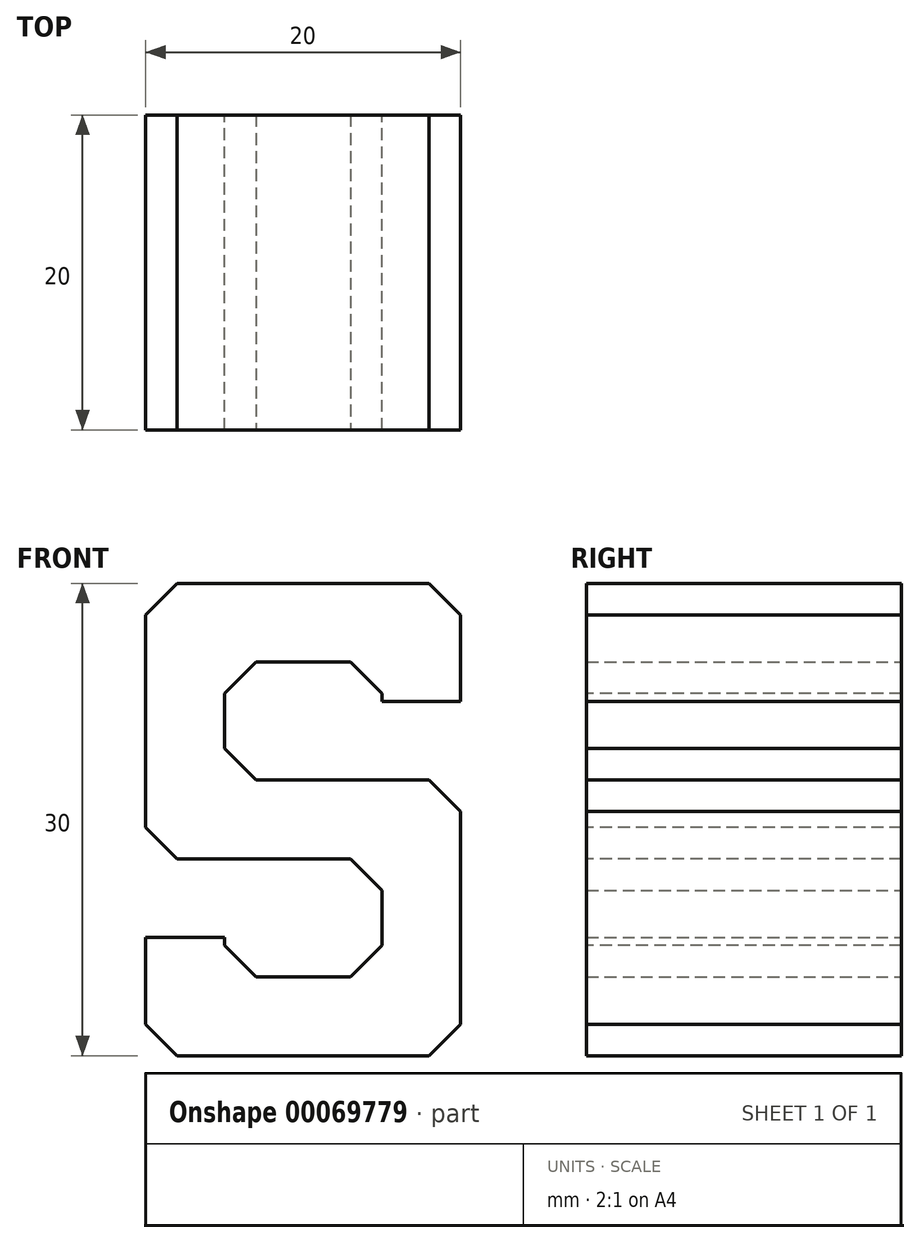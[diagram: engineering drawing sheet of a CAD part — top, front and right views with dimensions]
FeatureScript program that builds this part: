
annotation { "Feature Type Name" : "Feature", "Feature Type Description" : "" }
export const myFeature = defineFeature(function(context is Context, id is Id, definition is map)
    precondition{}
    {
        {
            var Q0;
            Q0=qCreatedBy(makeId("Front.planeOp"),FACE);
            var sketch = newSketch(context, id + "F0", { "sketchPlane" : qUnion([Q0])});
            skLineSegment(sketch, "E0.bottom", {"start": v(0, 0) * mm, "end": v(20, 0) * mm});
            skLineSegment(sketch, "E0.top", {"start": v(0, 30) * mm, "end": v(20, 30) * mm});
            skLineSegment(sketch, "E0.left", {"start": v(0, 0) * mm, "end": v(0, 7.5) * mm});
            skLineSegment(sketch, "E0.right", {"start": v(20, 0) * mm, "end": v(20, 17.5) * mm});
            skLineSegment(sketch, "E1", {"start": v(15, 25) * mm, "end": v(5, 25) * mm});
            skLineSegment(sketch, "E2", {"start": v(15, 25) * mm, "end": v(15, 22.5) * mm});
            skLineSegment(sketch, "E3", {"start": v(5, 25) * mm, "end": v(5, 17.5) * mm});
            skLineSegment(sketch, "E4", {"start": v(5, 5) * mm, "end": v(15, 5) * mm});
            skLineSegment(sketch, "E5", {"start": v(15, 22.5) * mm, "end": v(20, 22.5) * mm});
            skLineSegment(sketch, "E6", {"start": v(0, 7.5) * mm, "end": v(5, 7.5) * mm});
            skLineSegment(sketch, "E7.trimOffspring", {"start": v(15, 12.5) * mm, "end": v(15, 5) * mm});
            skLineSegment(sketch, "E8", {"start": v(5, 17.5) * mm, "end": v(20, 17.5) * mm});
            skLineSegment(sketch, "E9.trimOffspring", {"start": v(20, 22.5) * mm, "end": v(20, 30) * mm});
            skLineSegment(sketch, "E10", {"start": v(5, 7.5) * mm, "end": v(5, 5) * mm});
            skLineSegment(sketch, "E11", {"start": v(15, 12.5) * mm, "end": v(0, 12.5) * mm});
            skLineSegment(sketch, "E12.trimOffspring", {"start": v(0, 12.5) * mm, "end": v(0, 30) * mm});
            skSolve(sketch);
        }
        {
            var Q0;
            Q0=makeQuery(id+"F0.imprint","IMPRINT",FACE,{"disambiguationData":[TD([[makeQuery(id+"F0.imprint","IMPRINT",EDGE,{"derivedFrom":sQuery(id+"F0.wireOp",EDGE,"E0.bottom")}),1.0]])]});
            extrude(context, id + "F1", {"entities" : qUnion([Q0]), "depth" : 20 * mm});
        }
        {
            var Q0;
            Q0=makeQuery(id+"F1.opExtrude","SWEPT_EDGE",EDGE,{"disambiguationData":[OSD([sQuery(id+"F0.wireOp",EDGE,"E0.top"),sQuery(id+"F0.wireOp",EDGE,"E9.trimOffspring")])]});
            var Q1;
            Q1=makeQuery(id+"F1.opExtrude","SWEPT_EDGE",EDGE,{"disambiguationData":[OSD([sQuery(id+"F0.wireOp",EDGE,"E0.top"),sQuery(id+"F0.wireOp",EDGE,"E12.trimOffspring")])]});
            var Q2;
            Q2=makeQuery(id+"F1.opExtrude","SWEPT_EDGE",EDGE,{"disambiguationData":[OSD([sQuery(id+"F0.wireOp",EDGE,"E11"),sQuery(id+"F0.wireOp",EDGE,"E12.trimOffspring")])]});
            var Q3;
            Q3=makeQuery(id+"F1.opExtrude","SWEPT_EDGE",EDGE,{"disambiguationData":[OSD([sQuery(id+"F0.wireOp",EDGE,"E0.right"),sQuery(id+"F0.wireOp",EDGE,"E8")])]});
            var Q4;
            Q4=makeQuery(id+"F1.opExtrude","SWEPT_EDGE",EDGE,{"disambiguationData":[OSD([sQuery(id+"F0.wireOp",EDGE,"E0.bottom"),sQuery(id+"F0.wireOp",EDGE,"E0.left")])]});
            var Q5;
            Q5=makeQuery(id+"F1.opExtrude","SWEPT_EDGE",EDGE,{"disambiguationData":[OSD([sQuery(id+"F0.wireOp",EDGE,"E0.bottom"),sQuery(id+"F0.wireOp",EDGE,"E0.right")])]});
            chamfer(context, id + "F2", {"entities" : qUnion([Q0, Q1, Q2, Q3, Q4, Q5]), "width" : 2 * mm, "tangentPropagation" : true});
        }
        {
            var Q0;
            Q0=makeQuery(id+"F1.opExtrude","SWEPT_EDGE",EDGE,{"disambiguationData":[OSD([sQuery(id+"F0.wireOp",EDGE,"E3"),sQuery(id+"F0.wireOp",EDGE,"E8")])]});
            var Q1;
            Q1=makeQuery(id+"F1.opExtrude","SWEPT_EDGE",EDGE,{"disambiguationData":[OSD([sQuery(id+"F0.wireOp",EDGE,"E4"),sQuery(id+"F0.wireOp",EDGE,"E10")])]});
            var Q2;
            Q2=makeQuery(id+"F1.opExtrude","SWEPT_EDGE",EDGE,{"disambiguationData":[OSD([sQuery(id+"F0.wireOp",EDGE,"E1"),sQuery(id+"F0.wireOp",EDGE,"E3")])]});
            var Q3;
            Q3=makeQuery(id+"F1.opExtrude","SWEPT_EDGE",EDGE,{"disambiguationData":[OSD([sQuery(id+"F0.wireOp",EDGE,"E7.trimOffspring"),sQuery(id+"F0.wireOp",EDGE,"E11")])]});
            var Q4;
            Q4=makeQuery(id+"F1.opExtrude","SWEPT_EDGE",EDGE,{"disambiguationData":[OSD([sQuery(id+"F0.wireOp",EDGE,"E1"),sQuery(id+"F0.wireOp",EDGE,"E2")])]});
            var Q5;
            Q5=makeQuery(id+"F1.opExtrude","SWEPT_EDGE",EDGE,{"disambiguationData":[OSD([sQuery(id+"F0.wireOp",EDGE,"E4"),sQuery(id+"F0.wireOp",EDGE,"E7.trimOffspring")])]});
            chamfer(context, id + "F3", {"entities" : qUnion([Q0, Q1, Q2, Q3, Q4, Q5]), "width" : 2 * mm, "tangentPropagation" : true});
        }
    });
